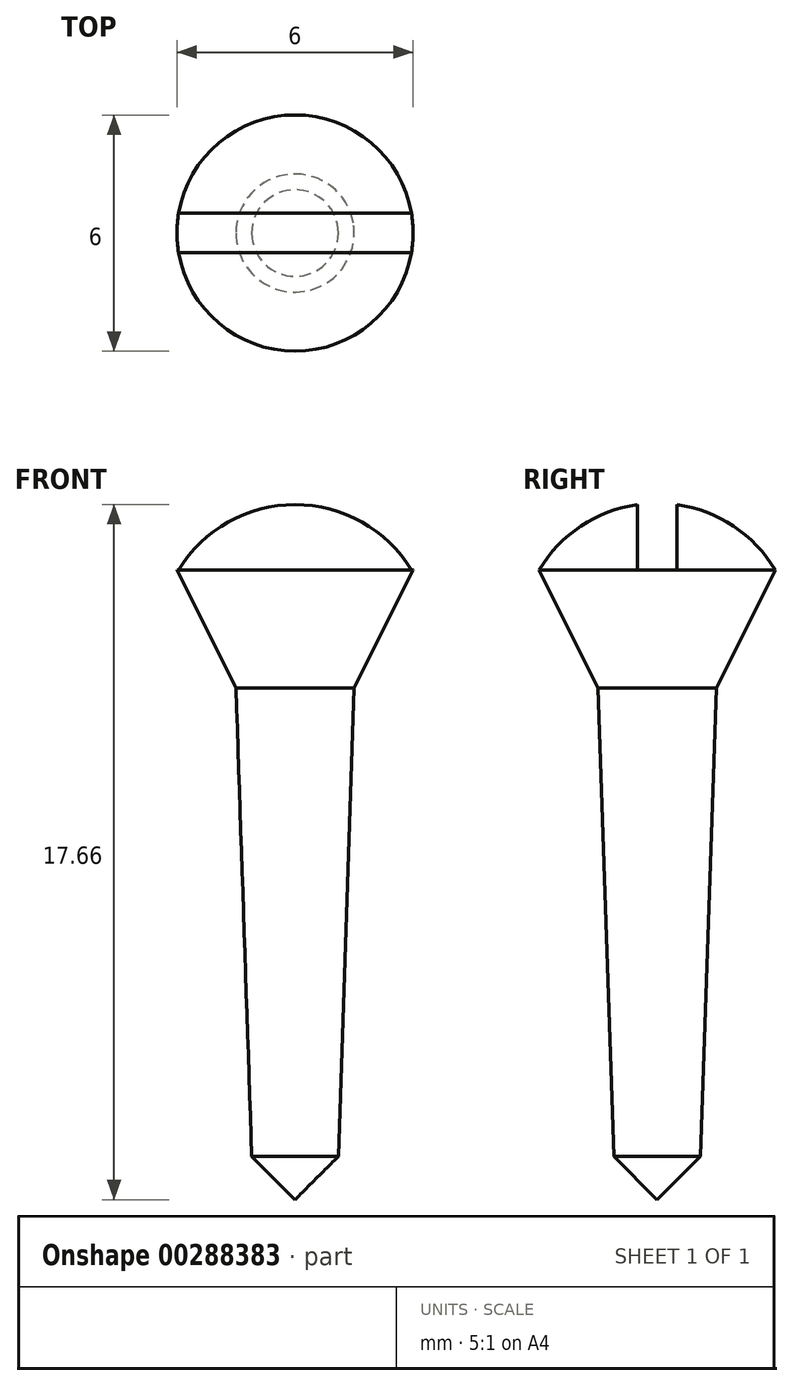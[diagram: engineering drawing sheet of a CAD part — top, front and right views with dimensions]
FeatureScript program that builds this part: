
annotation { "Feature Type Name" : "Feature", "Feature Type Description" : "" }
export const myFeature = defineFeature(function(context is Context, id is Id, definition is map)
    precondition{}
    {
        {
            var Q0;
            Q0=qCreatedBy(makeId("Front.planeOp"),FACE);
            var sketch = newSketch(context, id + "F0", { "sketchPlane" : qUnion([Q0])});
            skLineSegment(sketch, "E0", {"start": v(0, 0) * mm, "end": v(0, 17.7) * mm});
            skLineSegment(sketch, "E1", {"start": v(3, 16) * mm, "end": v(1.5, 13) * mm});
            skLineSegment(sketch, "E2", {"start": v(1.5, 13) * mm, "end": v(1.1, 1.1) * mm});
            skLineSegment(sketch, "E3", {"start": v(1.1, 1.1) * mm, "end": v(0, 0) * mm});
            skArc(sketch, "E4", {"start": v(3, 16) * mm, "mid": v(1.72, 17.24) * mm, "end": v(0, 17.7) * mm});
            skPoint(sketch, "E5.MirrorCS.start.orphan", {"position": v(0, 16) * mm});
            skPoint(sketch, "E6.orphan", {"position": v(-3, 16) * mm});
            skSolve(sketch);
        }
        {
            var Q0;
            Q0=makeQuery(id+"F0.imprint","IMPRINT",FACE,{"disambiguationData":[TD([[makeQuery(id+"F0.imprint","IMPRINT",EDGE,{"derivedFrom":sQuery(id+"F0.wireOp",EDGE,"E0")}),-1.0]])]});
            var Q1;
            Q1=sQuery(id+"F0.wireOp",EDGE,"E0");
            revolve(context, id + "F1", {"entities" : qUnion([Q0]), "axis" : qUnion([Q1]), "revolveType" : RevolveType.FULL});
        }
        {
            var Q0;
            Q0=qCreatedBy(makeId("Top.planeOp"),FACE);
            cPlane(context, id + "F2", {"entities" : qUnion([Q0]), "cplaneType" : CPlaneType.OFFSET, "offset" : 16 * mm, "width" : 150 * mm, "height" : 150 * mm});
        }
        {
            var Q0;
            Q0=qCreatedBy(id+"F2.planeOp",FACE);
            var sketch = newSketch(context, id + "F3", { "sketchPlane" : qUnion([Q0])});
            skLineSegment(sketch, "E7.bottom", {"start": v(4, 0.5) * mm, "end": v(-4, 0.5) * mm});
            skLineSegment(sketch, "E7.top", {"start": v(4, -0.5) * mm, "end": v(-4, -0.5) * mm});
            skLineSegment(sketch, "E7.left", {"start": v(4, 0.5) * mm, "end": v(4, -0.5) * mm});
            skLineSegment(sketch, "E7.right", {"start": v(-4, 0.5) * mm, "end": v(-4, -0.5) * mm});
            skPoint(sketch, "E7.middle", {"position": v(0, 0) * mm});
            skSolve(sketch);
        }
        {
            var Q0;
            Q0=qSketchRegion(id+"F3",true);
            extrude(context, id + "F4", {"entities" : qUnion([Q0]), "operationType" : NewBodyOperationType.REMOVE, "depth" : 2.4 * mm});
        }
    });
